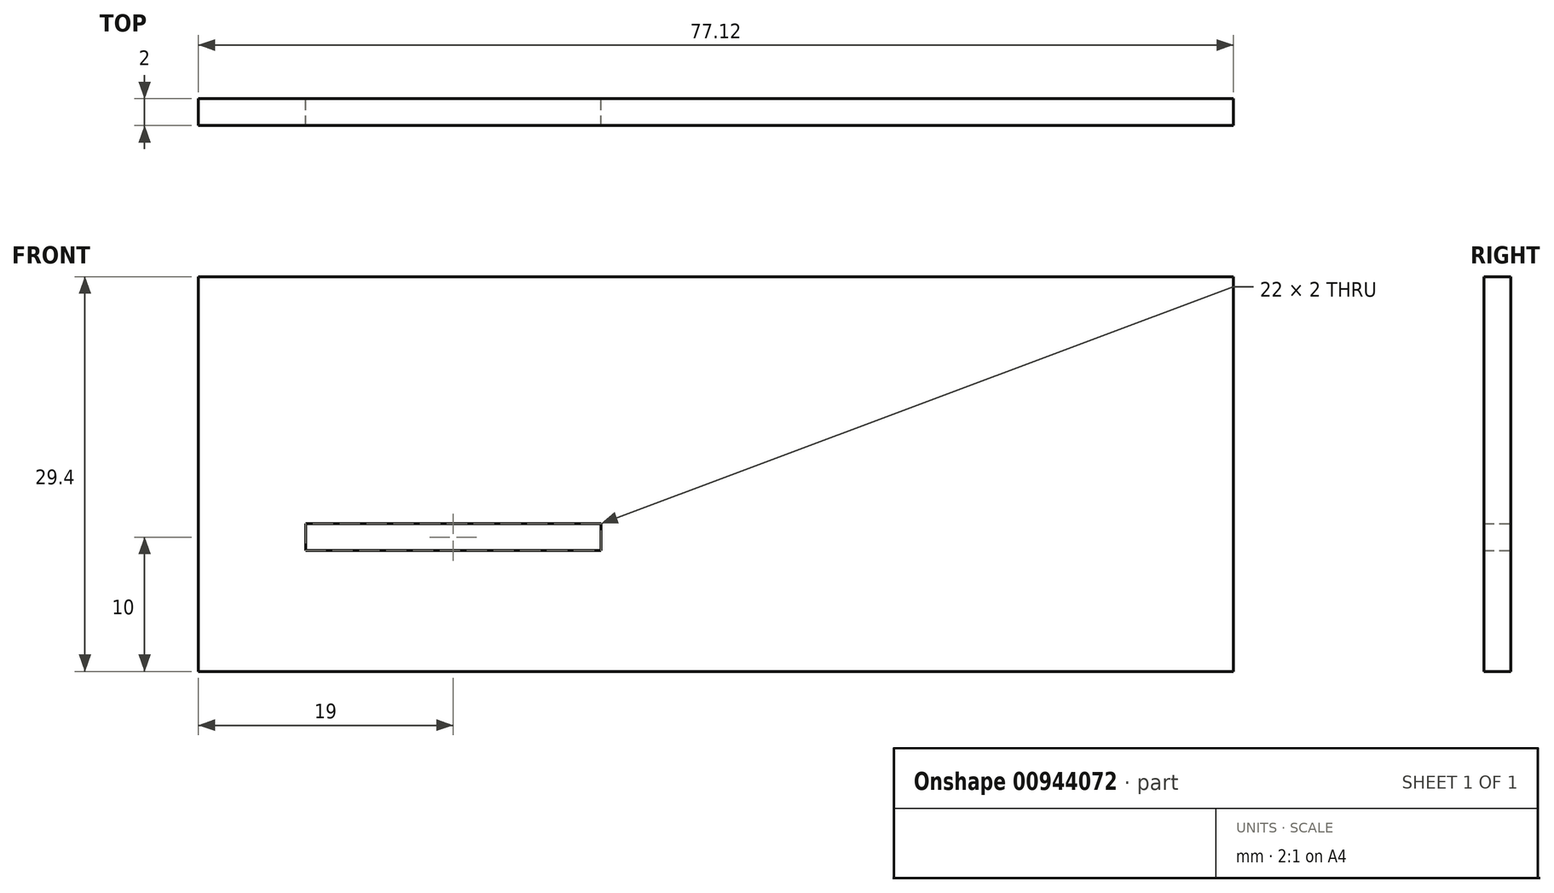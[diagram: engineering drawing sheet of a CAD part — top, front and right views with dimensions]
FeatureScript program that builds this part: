
annotation { "Feature Type Name" : "Feature", "Feature Type Description" : "" }
export const myFeature = defineFeature(function(context is Context, id is Id, definition is map)
    precondition{}
    {
        {
            var Q0;
            Q0=qCreatedBy(makeId("Front.planeOp"),FACE);
            var sketch = newSketch(context, id + "F0", { "sketchPlane" : qUnion([Q0])});
            skLineSegment(sketch, "E0.bottom", {"start": v(0, 29.4) * mm, "end": v(77.12, 29.4) * mm});
            skLineSegment(sketch, "E0.top", {"start": v(0, 0) * mm, "end": v(77.12, 0) * mm});
            skLineSegment(sketch, "E0.left", {"start": v(0, 29.4) * mm, "end": v(0, 0) * mm});
            skLineSegment(sketch, "E0.right", {"start": v(77.12, 29.4) * mm, "end": v(77.12, 0) * mm});
            skPoint(sketch, "E1", {"position": v(0, 0) * mm});
            skLineSegment(sketch, "E2.bottom", {"start": v(8, 11) * mm, "end": v(30, 11) * mm});
            skLineSegment(sketch, "E2.top", {"start": v(8, 9) * mm, "end": v(30, 9) * mm});
            skLineSegment(sketch, "E2.left", {"start": v(8, 11) * mm, "end": v(8, 9) * mm});
            skLineSegment(sketch, "E2.right", {"start": v(30, 11) * mm, "end": v(30, 9) * mm});
            skSolve(sketch);
        }
        {
            var Q0;
            Q0=makeQuery(id+"F0.imprint","IMPRINT",FACE,{"disambiguationData":[TD([[makeQuery(id+"F0.imprint","IMPRINT",EDGE,{"derivedFrom":sQuery(id+"F0.wireOp",EDGE,"E0.bottom")}),-1.0]])]});
            extrude(context, id + "F1", {"entities" : qUnion([Q0]), "depth" : 2 * mm, "offsetDistance" : 25 * mm});
        }
    });
